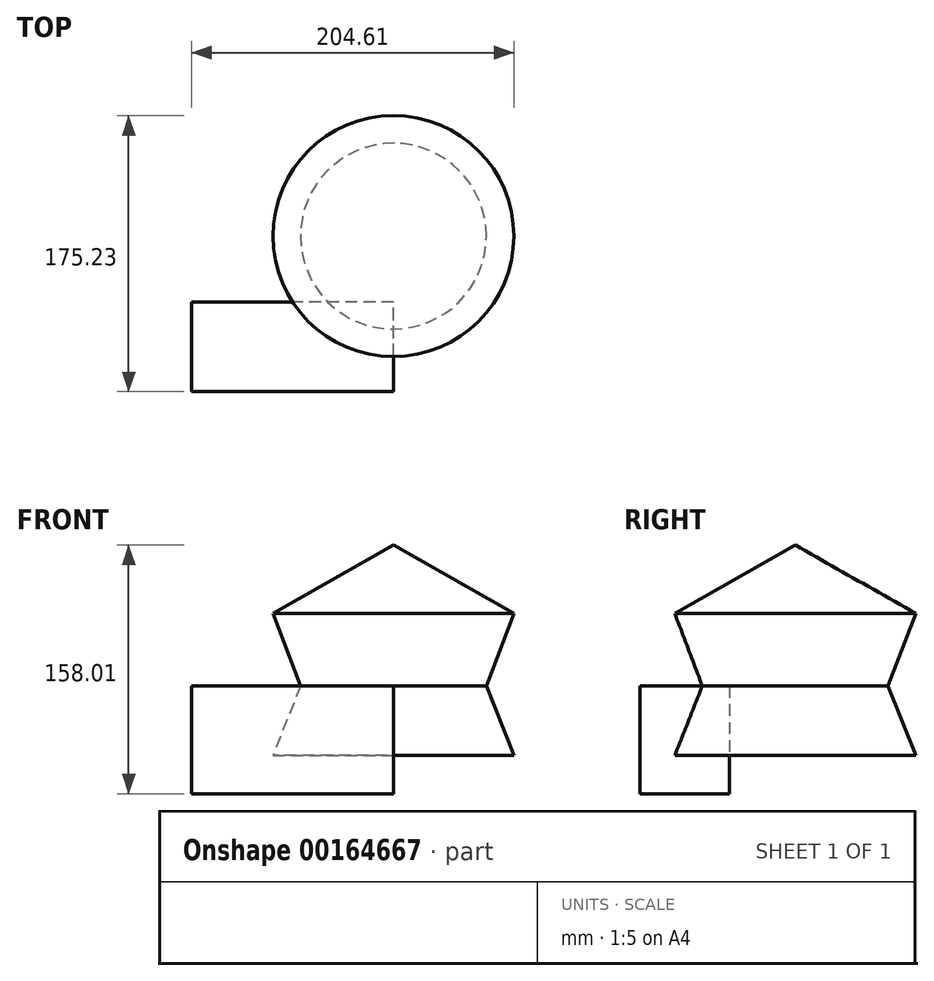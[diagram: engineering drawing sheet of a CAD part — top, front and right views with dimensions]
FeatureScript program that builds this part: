
annotation { "Feature Type Name" : "Feature", "Feature Type Description" : "" }
export const myFeature = defineFeature(function(context is Context, id is Id, definition is map)
    precondition{}
    {
        {
            var Q0;
            Q0=qCreatedBy(makeId("Front.planeOp"),FACE);
            var sketch = newSketch(context, id + "F0", { "sketchPlane" : qUnion([Q0])});
            skLineSegment(sketch, "E0.bottom", {"start": v(0, 0) * mm, "end": v(-128.1, 0) * mm});
            skLineSegment(sketch, "E0.top", {"start": v(0, -68.47) * mm, "end": v(-128.1, -68.47) * mm});
            skLineSegment(sketch, "E0.left", {"start": v(0, 0) * mm, "end": v(0, -68.47) * mm});
            skLineSegment(sketch, "E0.right", {"start": v(-128.1, 0) * mm, "end": v(-128.1, -68.47) * mm});
            skSolve(sketch);
        }
        {
            var Q0;
            Q0 = qSketchRegion(id + "F0", true);
            extrude(context, id + "F1", {"entities" : qUnion([Q0]), "depth" : 57 * mm});
        }
        {
            var Q0;
            Q0=qCreatedBy(makeId("Right.planeOp"),FACE);
            var sketch = newSketch(context, id + "F2", { "sketchPlane" : qUnion([Q0])});
            skLineSegment(sketch, "E1", {"start": v(41.72, 89.54) * mm, "end": v(41.72, -44.03) * mm});
            skLineSegment(sketch, "E2", {"start": v(41.72, -44.03) * mm, "end": v(118.23, -44.03) * mm});
            skLineSegment(sketch, "E3", {"start": v(118.23, -44.03) * mm, "end": v(100.7, 0) * mm});
            skLineSegment(sketch, "E4", {"start": v(100.7, 0) * mm, "end": v(118.23, 46.14) * mm});
            skLineSegment(sketch, "E5", {"start": v(118.23, 46.14) * mm, "end": v(41.72, 89.54) * mm});
            skSolve(sketch);
        }
        {
            var Q0;
            Q0 = qSketchRegion(id + "F2", true);
            var Q1;
            Q1=sQuery(id+"F2.wireOp",EDGE,"E1");
            revolve(context, id + "F3", {"entities" : qUnion([Q0]), "axis" : qUnion([Q1]), "revolveType" : RevolveType.FULL});
        }
    });
